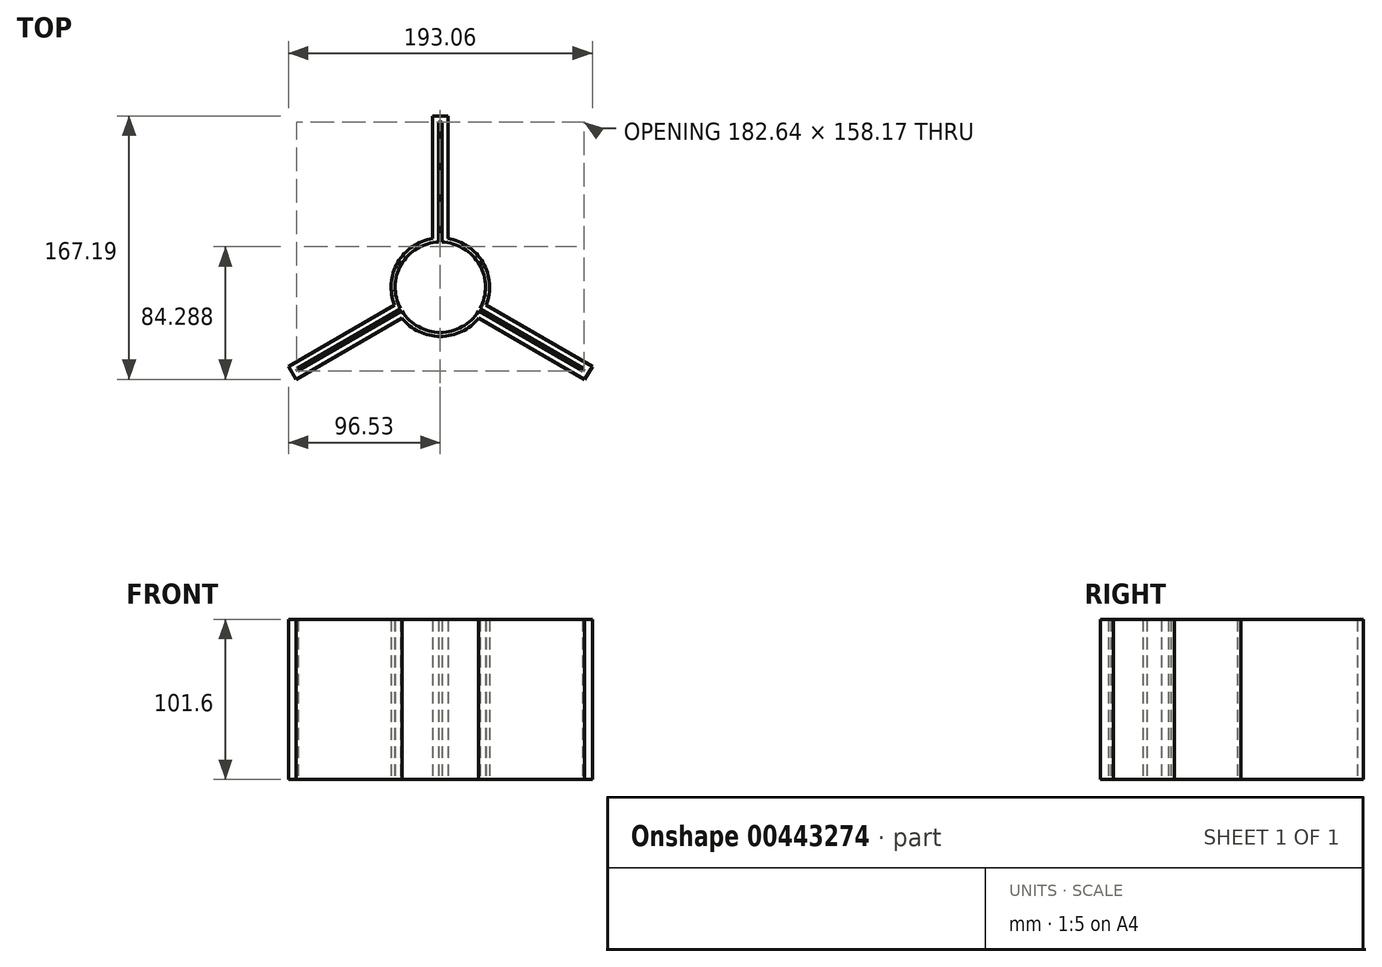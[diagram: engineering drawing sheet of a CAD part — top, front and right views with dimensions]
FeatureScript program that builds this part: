
annotation { "Feature Type Name" : "Feature", "Feature Type Description" : "" }
export const myFeature = defineFeature(function(context is Context, id is Id, definition is map)
    precondition{}
    {
        {
            var Q0;
            Q0=qCreatedBy(makeId("Top.planeOp"),FACE);
            var sketch = newSketch(context, id + "F0", { "sketchPlane" : qUnion([Q0])});
            skCircle(sketch, "E0", {"center": v(0, 0) * mm, "radius": 28.7 * mm});
            skCircle(sketch, "E1", {"center": v(0, 0) * mm, "radius": 31.24 * mm});
            skLineSegment(sketch, "E2.bottom", {"start": v(-0.98, 104.89) * mm, "end": v(0.98, 104.89) * mm});
            skLineSegment(sketch, "E2.top", {"start": v(-0.98, 28.69) * mm, "end": v(0.98, 28.69) * mm});
            skLineSegment(sketch, "E2.left", {"start": v(-0.98, 104.89) * mm, "end": v(-0.98, 28.69) * mm});
            skLineSegment(sketch, "E2.right", {"start": v(0.98, 104.89) * mm, "end": v(0.98, 28.69) * mm});
            skPoint(sketch, "E3", {"position": v(0, 28.69) * mm});
            skLineSegment(sketch, "E4.1.0", {"start": v(-90.34, -53.29) * mm, "end": v(-24.35, -15.19) * mm});
            skLineSegment(sketch, "E4.1.1", {"start": v(-90.34, -53.29) * mm, "end": v(-91.32, -51.6) * mm});
            skLineSegment(sketch, "E4.1.2", {"start": v(-91.32, -51.6) * mm, "end": v(-25.33, -13.5) * mm});
            skLineSegment(sketch, "E4.1.3", {"start": v(-24.35, -15.19) * mm, "end": v(-25.33, -13.5) * mm});
            skLineSegment(sketch, "E4.2.0", {"start": v(91.32, -51.6) * mm, "end": v(25.33, -13.5) * mm});
            skLineSegment(sketch, "E4.2.1", {"start": v(91.32, -51.6) * mm, "end": v(90.34, -53.29) * mm});
            skLineSegment(sketch, "E4.2.2", {"start": v(90.34, -53.29) * mm, "end": v(24.35, -15.19) * mm});
            skLineSegment(sketch, "E4.2.3", {"start": v(25.33, -13.5) * mm, "end": v(24.35, -15.19) * mm});
            skLineSegment(sketch, "E5.bottom", {"start": v(-4.79, 30.87) * mm, "end": v(4.79, 30.87) * mm});
            skLineSegment(sketch, "E5.top", {"start": v(-4.79, 108.7) * mm, "end": v(4.79, 108.7) * mm});
            skLineSegment(sketch, "E5.left", {"start": v(-4.79, 30.87) * mm, "end": v(-4.79, 108.7) * mm});
            skLineSegment(sketch, "E5.right", {"start": v(4.79, 30.87) * mm, "end": v(4.79, 108.7) * mm});
            skLineSegment(sketch, "E6.1.0", {"start": v(-24.34, -19.58) * mm, "end": v(-91.74, -58.5) * mm});
            skLineSegment(sketch, "E6.1.1", {"start": v(-91.74, -58.5) * mm, "end": v(-96.53, -50.2) * mm});
            skLineSegment(sketch, "E6.1.2", {"start": v(-29.13, -11.3) * mm, "end": v(-96.53, -50.2) * mm});
            skLineSegment(sketch, "E6.1.3", {"start": v(-24.34, -19.58) * mm, "end": v(-29.13, -11.3) * mm});
            skLineSegment(sketch, "E6.2.0", {"start": v(29.13, -11.3) * mm, "end": v(96.53, -50.2) * mm});
            skLineSegment(sketch, "E6.2.1", {"start": v(96.53, -50.2) * mm, "end": v(91.74, -58.5) * mm});
            skLineSegment(sketch, "E6.2.2", {"start": v(24.34, -19.58) * mm, "end": v(91.74, -58.5) * mm});
            skLineSegment(sketch, "E6.2.3", {"start": v(29.13, -11.3) * mm, "end": v(24.34, -19.58) * mm});
            skSolve(sketch);
        }
        {
            var Q0;
            {var subQ5=sQuery(id+"F0.wireOp",EDGE,"E2.left");var subQ7=sQuery(id+"F0.wireOp",EDGE,"E5.bottom");var subQ8=makeQuery(id+"F0.imprint","INTERSECT",VERTEX,{"derivedFrom":[subQ5,subQ7]});Q0=makeQuery(id+"F0.imprint","IMPRINT",FACE,{"disambiguationData":[TD([[makeQuery(id+"F0.imprint","IMPRINT",EDGE,{"disambiguationData":[TD([[subQ8,-1.0]])],"derivedFrom":subQ5}),-1.0]])]});}
            var Q1;
            {var subQ5=sQuery(id+"F0.wireOp",EDGE,"E2.right");var subQ7=sQuery(id+"F0.wireOp",EDGE,"E5.bottom");var subQ8=makeQuery(id+"F0.imprint","INTERSECT",VERTEX,{"derivedFrom":[subQ5,subQ7]});Q1=makeQuery(id+"F0.imprint","IMPRINT",FACE,{"disambiguationData":[TD([[makeQuery(id+"F0.imprint","IMPRINT",EDGE,{"disambiguationData":[TD([[subQ8,-1.0]])],"derivedFrom":subQ5}),1.0]])]});}
            var Q2;
            {var subQ1=sQuery(id+"F0.wireOp",EDGE,"E2.bottom");Q2=makeQuery(id+"F0.imprint","IMPRINT",FACE,{"disambiguationData":[TD([[makeQuery(id+"F0.imprint","IMPRINT",EDGE,{"derivedFrom":subQ1}),1.0]])]});}
            var Q3;
            {var subQ5=sQuery(id+"F0.wireOp",EDGE,"E6.1.3");var subQ8=sQuery(id+"F0.wireOp",EDGE,"E4.1.0");var subQ9=makeQuery(id+"F0.imprint","INTERSECT",VERTEX,{"derivedFrom":[subQ8,subQ5]});Q3=makeQuery(id+"F0.imprint","IMPRINT",FACE,{"disambiguationData":[TD([[makeQuery(id+"F0.imprint","IMPRINT",EDGE,{"disambiguationData":[TD([[subQ9,-1.0]])],"derivedFrom":subQ8}),-1.0]])]});}
            var Q4;
            {var subQ0=sQuery(id+"F0.wireOp",EDGE,"E4.2.1");Q4=makeQuery(id+"F0.imprint","IMPRINT",FACE,{"disambiguationData":[TD([[makeQuery(id+"F0.imprint","IMPRINT",EDGE,{"derivedFrom":subQ0}),1.0]])]});}
            var Q5;
            {var subQ0=sQuery(id+"F0.wireOp",EDGE,"E4.1.1");Q5=makeQuery(id+"F0.imprint","IMPRINT",FACE,{"disambiguationData":[TD([[makeQuery(id+"F0.imprint","IMPRINT",EDGE,{"derivedFrom":subQ0}),1.0]])]});}
            var Q6;
            {var subQ1=sQuery(id+"F0.wireOp",EDGE,"E1");var subQ3=sQuery(id+"F0.wireOp",EDGE,"E2.right");var subQ4=makeQuery(id+"F0.imprint","INTERSECT",VERTEX,{"derivedFrom":[subQ1,subQ3]});Q6=makeQuery(id+"F0.imprint","IMPRINT",FACE,{"disambiguationData":[TD([[makeQuery(id+"F0.imprint","IMPRINT",EDGE,{"disambiguationData":[TD([[subQ4,-1.0]])],"derivedFrom":subQ3}),1.0]])]});}
            var Q7;
            {var subQ1=sQuery(id+"F0.wireOp",EDGE,"E1");var subQ3=sQuery(id+"F0.wireOp",EDGE,"E2.left");var subQ4=makeQuery(id+"F0.imprint","INTERSECT",VERTEX,{"derivedFrom":[subQ1,subQ3]});Q7=makeQuery(id+"F0.imprint","IMPRINT",FACE,{"disambiguationData":[TD([[makeQuery(id+"F0.imprint","IMPRINT",EDGE,{"disambiguationData":[TD([[subQ4,-1.0]])],"derivedFrom":subQ3}),-1.0]])]});}
            var Q8;
            {var subQ1=sQuery(id+"F0.wireOp",EDGE,"E1");var subQ3=sQuery(id+"F0.wireOp",EDGE,"E4.2.0");var subQ4=makeQuery(id+"F0.imprint","INTERSECT",VERTEX,{"derivedFrom":[subQ1,subQ3]});Q8=makeQuery(id+"F0.imprint","IMPRINT",FACE,{"disambiguationData":[TD([[makeQuery(id+"F0.imprint","IMPRINT",EDGE,{"disambiguationData":[TD([[subQ4,-1.0]])],"derivedFrom":subQ3}),-1.0]])]});}
            var Q9;
            {var subQ1=sQuery(id+"F0.wireOp",EDGE,"E1");var subQ3=sQuery(id+"F0.wireOp",EDGE,"E4.2.2");var subQ4=makeQuery(id+"F0.imprint","INTERSECT",VERTEX,{"derivedFrom":[subQ1,subQ3]});Q9=makeQuery(id+"F0.imprint","IMPRINT",FACE,{"disambiguationData":[TD([[makeQuery(id+"F0.imprint","IMPRINT",EDGE,{"disambiguationData":[TD([[subQ4,-1.0]])],"derivedFrom":subQ3}),1.0]])]});}
            var Q10;
            {var subQ1=sQuery(id+"F0.wireOp",EDGE,"E1");var subQ3=sQuery(id+"F0.wireOp",EDGE,"E4.1.0");var subQ4=makeQuery(id+"F0.imprint","INTERSECT",VERTEX,{"derivedFrom":[subQ1,subQ3]});Q10=makeQuery(id+"F0.imprint","IMPRINT",FACE,{"disambiguationData":[TD([[makeQuery(id+"F0.imprint","IMPRINT",EDGE,{"disambiguationData":[TD([[subQ4,-1.0]])],"derivedFrom":subQ3}),-1.0]])]});}
            var Q11;
            {var subQ1=sQuery(id+"F0.wireOp",EDGE,"E1");var subQ3=sQuery(id+"F0.wireOp",EDGE,"E4.1.2");var subQ4=makeQuery(id+"F0.imprint","INTERSECT",VERTEX,{"derivedFrom":[subQ1,subQ3]});Q11=makeQuery(id+"F0.imprint","IMPRINT",FACE,{"disambiguationData":[TD([[makeQuery(id+"F0.imprint","IMPRINT",EDGE,{"disambiguationData":[TD([[subQ4,-1.0]])],"derivedFrom":subQ3}),1.0]])]});}
            extrude(context, id + "F1", {"entities" : qUnion([Q0, Q1, Q2, Q3, Q4, Q5, Q6, Q7, Q8, Q9, Q10, Q11]), "depth" : 101.6 * mm});
        }
    });
